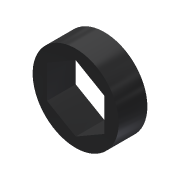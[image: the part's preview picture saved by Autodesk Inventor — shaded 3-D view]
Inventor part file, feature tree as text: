
AUTODESK INVENTOR PART (.ipt)
format: ipt  version: 2013 (Build 170138000, 138)  size: 79,872 bytes
history: native  units: in
note: dims shown in document units (in); Inventor stores cm internally (conversion verified against a paired STEP export)
features: extrude x1, sketch x1
ambient origin geometry x8: Origin, YZ Plane, XZ Plane, XY Plane, X Axis, Y Axis, Z Axis, Center Point
bodies: Solid1 (feature_tree)
feature tree (2):
  extrude  "Extrusion1"  Depth=0.5in
  sketch  "Sketch1"  dims[d0=0.75in d2=0.5in d3=0.25in d4=0.0in]
